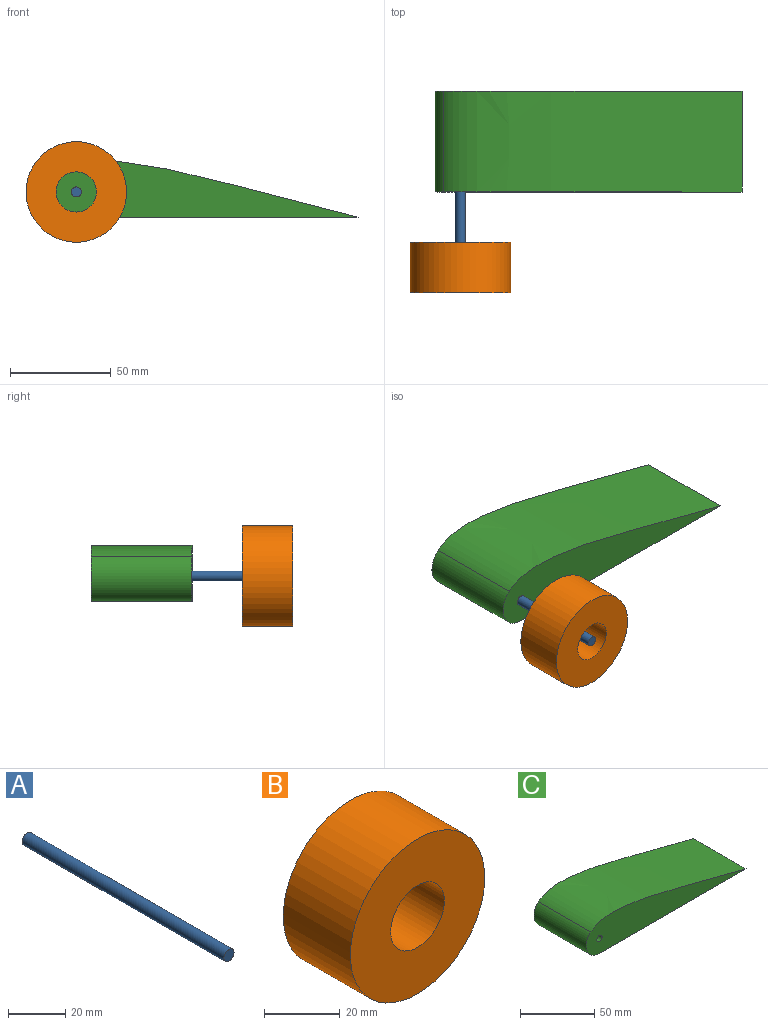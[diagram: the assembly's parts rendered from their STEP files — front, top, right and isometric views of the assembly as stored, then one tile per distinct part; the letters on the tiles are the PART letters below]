
ASSEMBLY  parts=3 mates=2
PART A: 3 faces, bbox 5x100x5 mm
  f0: cylinder r=2.5mm len=100mm, axis (0,1,0), area 1570.8mm2, adj f1,f2
  f1: plane 5x5mm, normal (0,-1,0), area 19.6mm2, adj f0
  f2: plane 5x5mm, normal (0,1,0), area 19.6mm2, adj f0
PART B: 4 faces, bbox 50x25x50 mm
  f0: cylinder r=10mm len=25mm, axis (0,1,0), area 1570.8mm2, adj f2,f3
  f1: cylinder r=25mm len=50mm, axis (0,1,0), area 3927mm2, adj f2,f3
  f2: plane 50x50mm, normal (0,-1,0), area 1649.3mm2, adj f0,f1
  f3: plane 50x50mm, normal (0,1,0), area 1649.3mm2, adj f0,f1
PART C: 6 faces, bbox 152.5x50x33.4 mm
  f0: extruded ~148.2x50mm, area 7636.3mm2, adj f1,f3,f4,f5
  f1: cylinder r=12.5mm len=50mm, axis (0,1,0), area 1516.3mm2, adj f0,f3,f4,f5
  f2: cylinder r=2.5mm len=50mm, axis (0,1,0), area 785.4mm2, adj f4,f5
  f3: plane 140x50mm, normal (0,0,-1), area 7000mm2, adj f0,f1,f4,f5
  f4: plane 152.5x33.37mm, normal (0,-1,0), area 2585.3mm2, adj f0,f1,f2,f3
  f5: plane 152.5x33.37mm, normal (0,1,0), area 2585.3mm2, adj f0,f1,f2,f3
PLACE A t=(-31.62,1.16,-20.87)mm
PLACE B rot(axis=(0,1,0),0deg) t=(-31.62,-36.34,-20.87)mm
PLACE C t=(29.94,26.16,-20.87)mm
MATE fastened A.f0 <-> B.f1  axis (0,-1,0) through (-31.62,-48.84,-20.87)mm
MATE fastened A.f0 <-> C.f2  axis (0,1,0) through (-31.62,51.16,-20.87)mm
